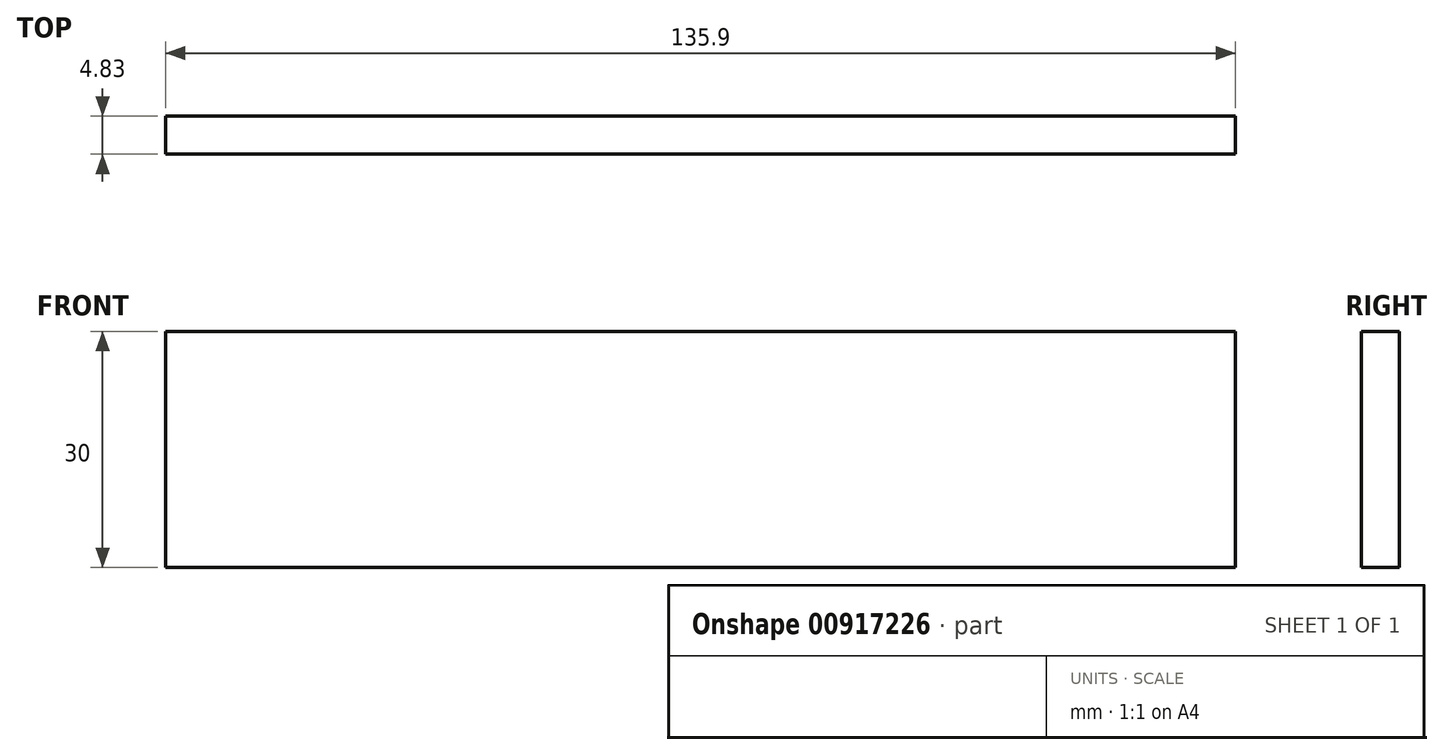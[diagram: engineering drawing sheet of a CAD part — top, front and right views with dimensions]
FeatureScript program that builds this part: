
annotation { "Feature Type Name" : "Feature", "Feature Type Description" : "" }
export const myFeature = defineFeature(function(context is Context, id is Id, definition is map)
    precondition{}
    {
        {
            var Q0;
            Q0=qCreatedBy(makeId("Front.planeOp"),FACE);
            var sketch = newSketch(context, id + "F0", { "sketchPlane" : qUnion([Q0])});
            skLineSegment(sketch, "E0.bottom", {"start": v(67.95, 15) * mm, "end": v(-67.95, 15) * mm});
            skLineSegment(sketch, "E0.top", {"start": v(67.95, -15) * mm, "end": v(-67.95, -15) * mm});
            skLineSegment(sketch, "E0.left", {"start": v(67.95, 15) * mm, "end": v(67.95, -15) * mm});
            skLineSegment(sketch, "E0.right", {"start": v(-67.95, 15) * mm, "end": v(-67.95, -15) * mm});
            skPoint(sketch, "E0.middle", {"position": v(0, 0) * mm});
            skSolve(sketch);
        }
        {
            var Q0;
            Q0=makeQuery(id+"F0.imprint","IMPRINT",FACE,{"disambiguationData":[TD([[makeQuery(id+"F0.imprint","IMPRINT",EDGE,{"derivedFrom":sQuery(id+"F0.wireOp",EDGE,"E0.bottom")}),1.0]])]});
            extrude(context, id + "F1", {"entities" : qUnion([Q0]), "depth" : 4.83 * mm, "offsetDistance" : 25 * mm});
        }
    });
